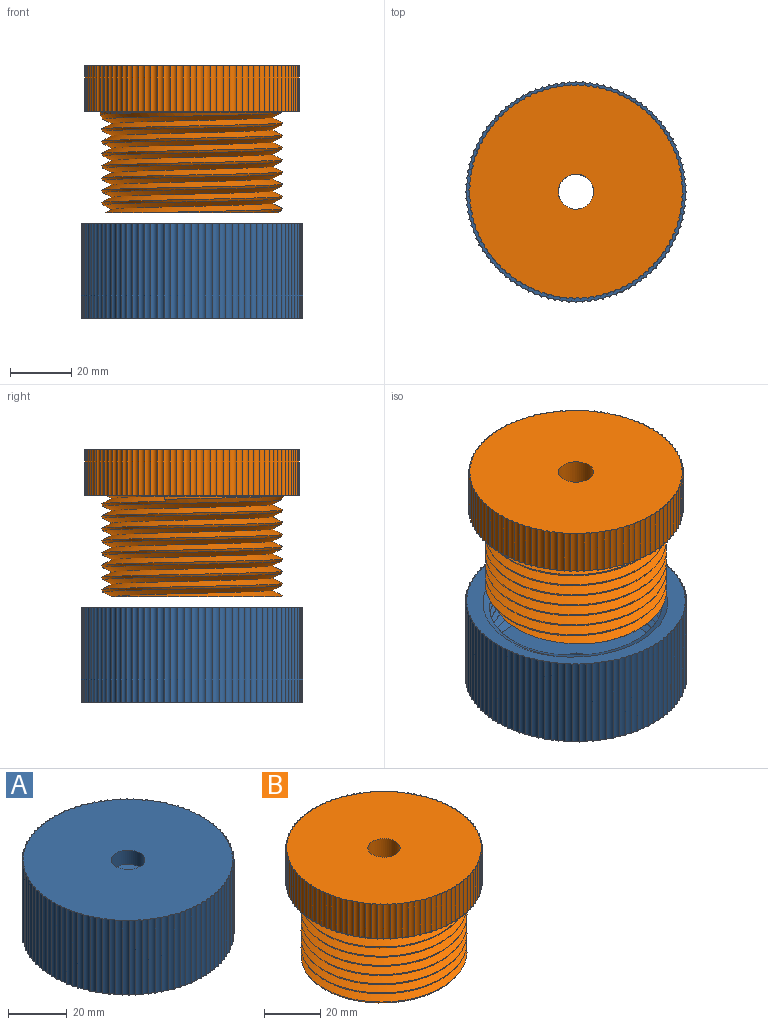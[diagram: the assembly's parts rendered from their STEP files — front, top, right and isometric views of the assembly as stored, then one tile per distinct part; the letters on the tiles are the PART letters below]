
ASSEMBLY  parts=2 mates=1
PART A: 107 faces, bbox 72.2x74.2x33.3 mm
  f0: bspline ~74.25x64.3mm, area 5175.7mm2, adj f1,f2,f3,f105
  f1: bspline ~74.25x64.3mm, area 5174.9mm2, adj f0,f2,f3,f105
  f2: cylinder r=28.25mm len=56.5mm, axis (0,0,-1), area 62.6mm2, adj f0,f1,f3,f105
  f3: plane 72.21x72.21mm, normal (0,0,-1), area 1161.6mm2, adj f0,f1,f2,f5,f6,f7,f8,f9
  f4: plane 72.21x72.21mm, normal (0,0,1), area 3917.8mm2, adj f5,f6,f7,f8,f9,f10,f11,f12
  f5: cylinder r=1.62mm len=31mm, axis (0,0,1), area 77.9mm2, adj f3,f4,f6,f104
  f6: cylinder r=1.62mm len=31mm, axis (0,0,1), area 77.9mm2, adj f3,f4,f5,f7
  f7: cylinder r=1.62mm len=31mm, axis (0,0,1), area 77.9mm2, adj f3,f4,f6,f8
  f8: cylinder r=1.62mm len=31mm, axis (0,0,1), area 77.9mm2, adj f3,f4,f7,f9
  f9: cylinder r=1.62mm len=31mm, axis (0,0,1), area 77.9mm2, adj f3,f4,f8,f10
  f10: cylinder r=1.62mm len=31mm, axis (0,0,1), area 77.9mm2, adj f3,f4,f9,f11
  f11: cylinder r=1.62mm len=31mm, axis (0,0,1), area 77.9mm2, adj f3,f4,f10,f12
  f12: cylinder r=1.62mm len=31mm, axis (0,0,1), area 77.9mm2, adj f3,f4,f11,f13
  f13: cylinder r=1.62mm len=31mm, axis (0,0,1), area 77.9mm2, adj f3,f4,f12,f14
  f14: cylinder r=1.62mm len=31mm, axis (0,0,1), area 77.9mm2, adj f3,f4,f13,f15
  f15: cylinder r=1.62mm len=31mm, axis (0,0,1), area 77.9mm2, adj f3,f4,f14,f16
  f16: cylinder r=1.62mm len=31mm, axis (0,0,1), area 77.9mm2, adj f3,f4,f15,f17
  f17: cylinder r=1.62mm len=31mm, axis (0,0,1), area 77.9mm2, adj f3,f4,f16,f18
  f18: cylinder r=1.62mm len=31mm, axis (0,0,1), area 77.9mm2, adj f3,f4,f17,f19
  f19: cylinder r=1.62mm len=31mm, axis (0,0,1), area 77.9mm2, adj f3,f4,f18,f20
  f20: cylinder r=1.62mm len=31mm, axis (0,0,1), area 77.9mm2, adj f3,f4,f19,f21
  f21: cylinder r=1.62mm len=31mm, axis (0,0,1), area 77.9mm2, adj f3,f4,f20,f22
  f22: cylinder r=1.62mm len=31mm, axis (0,0,1), area 77.9mm2, adj f3,f4,f21,f23
  f23: cylinder r=1.62mm len=31mm, axis (0,0,1), area 77.9mm2, adj f3,f4,f22,f24
  f24: cylinder r=1.62mm len=31mm, axis (0,0,1), area 77.9mm2, adj f3,f4,f23,f25
  f25: cylinder r=1.62mm len=31mm, axis (0,0,1), area 77.9mm2, adj f3,f4,f24,f26
  f26: cylinder r=1.62mm len=31mm, axis (0,0,1), area 77.9mm2, adj f3,f4,f25,f27
  f27: cylinder r=1.62mm len=31mm, axis (0,0,1), area 77.9mm2, adj f3,f4,f26,f28
  f28: cylinder r=1.62mm len=31mm, axis (0,0,1), area 77.9mm2, adj f3,f4,f27,f29
  f29: cylinder r=1.62mm len=31mm, axis (0,0,1), area 77.9mm2, adj f3,f4,f28,f30
  f30: cylinder r=1.62mm len=31mm, axis (0,0,1), area 77.9mm2, adj f3,f4,f29,f31
  f31: cylinder r=1.62mm len=31mm, axis (0,0,1), area 77.9mm2, adj f3,f4,f30,f32
  f32: cylinder r=1.62mm len=31mm, axis (0,0,1), area 77.9mm2, adj f3,f4,f31,f33
  f33: cylinder r=1.62mm len=31mm, axis (0,0,1), area 77.9mm2, adj f3,f4,f32,f34
  f34: cylinder r=1.62mm len=31mm, axis (0,0,1), area 77.9mm2, adj f3,f4,f33,f35
  f35: cylinder r=1.62mm len=31mm, axis (0,0,1), area 77.9mm2, adj f3,f4,f34,f36
  f36: cylinder r=1.62mm len=31mm, axis (0,0,1), area 77.9mm2, adj f3,f4,f35,f37
  f37: cylinder r=1.62mm len=31mm, axis (0,0,1), area 77.9mm2, adj f3,f4,f36,f38
  f38: cylinder r=1.62mm len=31mm, axis (0,0,1), area 77.9mm2, adj f3,f4,f37,f39
  f39: cylinder r=1.62mm len=31mm, axis (0,0,1), area 77.9mm2, adj f3,f4,f38,f40
  f40: cylinder r=1.62mm len=31mm, axis (0,0,1), area 77.9mm2, adj f3,f4,f39,f41
  f41: cylinder r=1.62mm len=31mm, axis (0,0,1), area 77.9mm2, adj f3,f4,f40,f42
  f42: cylinder r=1.62mm len=31mm, axis (0,0,1), area 77.9mm2, adj f3,f4,f41,f43
  f43: cylinder r=1.62mm len=31mm, axis (0,0,1), area 77.9mm2, adj f3,f4,f42,f44
  f44: cylinder r=1.62mm len=31mm, axis (0,0,1), area 77.9mm2, adj f3,f4,f43,f45
  f45: cylinder r=1.62mm len=31mm, axis (0,0,1), area 77.9mm2, adj f3,f4,f44,f46
  f46: cylinder r=1.62mm len=31mm, axis (0,0,1), area 77.9mm2, adj f3,f4,f45,f47
  f47: cylinder r=1.62mm len=31mm, axis (0,0,1), area 77.9mm2, adj f3,f4,f46,f48
  f48: cylinder r=1.62mm len=31mm, axis (0,0,1), area 77.9mm2, adj f3,f4,f47,f49
  f49: cylinder r=1.62mm len=31mm, axis (0,0,1), area 77.9mm2, adj f3,f4,f48,f50
  f50: cylinder r=1.62mm len=31mm, axis (0,0,1), area 77.9mm2, adj f3,f4,f49,f51
  f51: cylinder r=1.62mm len=31mm, axis (0,0,1), area 77.9mm2, adj f3,f4,f50,f52
  f52: cylinder r=1.62mm len=31mm, axis (0,0,1), area 77.9mm2, adj f3,f4,f51,f53
  f53: cylinder r=1.62mm len=31mm, axis (0,0,1), area 77.9mm2, adj f3,f4,f52,f54
  f54: cylinder r=1.62mm len=31mm, axis (0,0,1), area 77.9mm2, adj f3,f4,f53,f55
  f55: cylinder r=1.62mm len=31mm, axis (0,0,1), area 77.9mm2, adj f3,f4,f54,f56
  f56: cylinder r=1.62mm len=31mm, axis (0,0,1), area 77.9mm2, adj f3,f4,f55,f57
  f57: cylinder r=1.62mm len=31mm, axis (0,0,1), area 77.9mm2, adj f3,f4,f56,f58
  f58: cylinder r=1.62mm len=31mm, axis (0,0,1), area 77.9mm2, adj f3,f4,f57,f59
  f59: cylinder r=1.62mm len=31mm, axis (0,0,1), area 77.9mm2, adj f3,f4,f58,f60
  f60: cylinder r=1.62mm len=31mm, axis (0,0,1), area 77.9mm2, adj f3,f4,f59,f61
  f61: cylinder r=1.62mm len=31mm, axis (0,0,1), area 77.9mm2, adj f3,f4,f60,f62
  f62: cylinder r=1.62mm len=31mm, axis (0,0,1), area 77.9mm2, adj f3,f4,f61,f63
  f63: cylinder r=1.62mm len=31mm, axis (0,0,1), area 77.9mm2, adj f3,f4,f62,f64
  f64: cylinder r=1.62mm len=31mm, axis (0,0,1), area 77.9mm2, adj f3,f4,f63,f65
  f65: cylinder r=1.62mm len=31mm, axis (0,0,1), area 77.9mm2, adj f3,f4,f64,f66
  f66: cylinder r=1.62mm len=31mm, axis (0,0,1), area 77.9mm2, adj f3,f4,f65,f67
  f67: cylinder r=1.62mm len=31mm, axis (0,0,1), area 77.9mm2, adj f3,f4,f66,f68
  f68: cylinder r=1.62mm len=31mm, axis (0,0,1), area 77.9mm2, adj f3,f4,f67,f69
  f69: cylinder r=1.62mm len=31mm, axis (0,0,1), area 77.9mm2, adj f3,f4,f68,f70
  f70: cylinder r=1.62mm len=31mm, axis (0,0,1), area 77.9mm2, adj f3,f4,f69,f71
  f71: cylinder r=1.62mm len=31mm, axis (0,0,1), area 77.9mm2, adj f3,f4,f70,f72
  f72: cylinder r=1.62mm len=31mm, axis (0,0,1), area 77.9mm2, adj f3,f4,f71,f73
  f73: cylinder r=1.62mm len=31mm, axis (0,0,1), area 77.9mm2, adj f3,f4,f72,f74
  f74: cylinder r=1.62mm len=31mm, axis (0,0,1), area 77.9mm2, adj f3,f4,f73,f75
  f75: cylinder r=1.62mm len=31mm, axis (0,0,1), area 77.9mm2, adj f3,f4,f74,f76
  f76: cylinder r=1.62mm len=31mm, axis (0,0,1), area 77.9mm2, adj f3,f4,f75,f77
  f77: cylinder r=1.62mm len=31mm, axis (0,0,1), area 77.9mm2, adj f3,f4,f76,f78
  f78: cylinder r=1.62mm len=31mm, axis (0,0,1), area 77.9mm2, adj f3,f4,f77,f79
  f79: cylinder r=1.62mm len=31mm, axis (0,0,1), area 77.9mm2, adj f3,f4,f78,f80
  f80: cylinder r=1.62mm len=31mm, axis (0,0,1), area 77.9mm2, adj f3,f4,f79,f81
  f81: cylinder r=1.62mm len=31mm, axis (0,0,1), area 77.9mm2, adj f3,f4,f80,f82
  f82: cylinder r=1.62mm len=31mm, axis (0,0,1), area 77.9mm2, adj f3,f4,f81,f83
  f83: cylinder r=1.62mm len=31mm, axis (0,0,1), area 77.9mm2, adj f3,f4,f82,f84
  f84: cylinder r=1.62mm len=31mm, axis (0,0,1), area 77.9mm2, adj f3,f4,f83,f85
  f85: cylinder r=1.62mm len=31mm, axis (0,0,1), area 77.9mm2, adj f3,f4,f84,f86
  f86: cylinder r=1.62mm len=31mm, axis (0,0,1), area 77.9mm2, adj f3,f4,f85,f87
  f87: cylinder r=1.62mm len=31mm, axis (0,0,1), area 77.9mm2, adj f3,f4,f86,f88
  f88: cylinder r=1.62mm len=31mm, axis (0,0,1), area 77.9mm2, adj f3,f4,f87,f89
  f89: cylinder r=1.62mm len=31mm, axis (0,0,1), area 77.9mm2, adj f3,f4,f88,f90
  f90: cylinder r=1.62mm len=31mm, axis (0,0,1), area 77.9mm2, adj f3,f4,f89,f91
  f91: cylinder r=1.62mm len=31mm, axis (0,0,1), area 77.9mm2, adj f3,f4,f90,f92
  f92: cylinder r=1.62mm len=31mm, axis (0,0,1), area 77.9mm2, adj f3,f4,f91,f93
  f93: cylinder r=1.62mm len=31mm, axis (0,0,1), area 77.9mm2, adj f3,f4,f92,f94
  f94: cylinder r=1.62mm len=31mm, axis (0,0,1), area 77.9mm2, adj f3,f4,f93,f95
  f95: cylinder r=1.62mm len=31mm, axis (0,0,1), area 77.9mm2, adj f3,f4,f94,f96
  f96: cylinder r=1.62mm len=31mm, axis (0,0,1), area 77.9mm2, adj f3,f4,f95,f97
  f97: cylinder r=1.62mm len=31mm, axis (0,0,1), area 77.9mm2, adj f3,f4,f96,f98
  f98: cylinder r=1.62mm len=31mm, axis (0,0,1), area 77.9mm2, adj f3,f4,f97,f99
  f99: cylinder r=1.62mm len=31mm, axis (0,0,1), area 77.9mm2, adj f3,f4,f98,f100
  f100: cylinder r=1.62mm len=31mm, axis (0,0,1), area 77.9mm2, adj f3,f4,f99,f101
  f101: cylinder r=1.62mm len=31mm, axis (0,0,1), area 77.9mm2, adj f3,f4,f100,f102
  f102: cylinder r=1.62mm len=31mm, axis (0,0,1), area 77.9mm2, adj f3,f4,f101,f103
  f103: cylinder r=1.62mm len=31mm, axis (0,0,1), area 77.9mm2, adj f3,f4,f102,f104
  f104: cylinder r=1.62mm len=31mm, axis (0,0,1), area 77.9mm2, adj f3,f4,f5,f103
  f105: plane 60.4x60.37mm, normal (0,0,-1), area 2756.4mm2, adj f0,f1,f2,f106
  f106: cylinder r=5.75mm len=11.5mm, axis (0,0,1), area 216.8mm2, adj f4,f105
PART B: 195 faces, bbox 72.6x72.6x52.9 mm
  f0: cylinder r=1.62mm len=0.9mm, axis (0,0,1), area 0.1mm2, adj f26,f76,f85,f92
  f1: cylinder r=1.62mm len=1.8mm, axis (0,0,1), area 0.2mm2, adj f2,f74,f85,f92
  f2: cylinder r=1.62mm len=1.8mm, axis (0,0,1), area 0.2mm2, adj f1,f3,f85,f92
  f3: cylinder r=1.62mm len=1.8mm, axis (0,0,1), area 0.2mm2, adj f2,f4,f85,f92
  f4: cylinder r=1.62mm len=1.78mm, axis (0,0,1), area 0.2mm2, adj f3,f5,f85,f92
  f5: cylinder r=1.62mm len=1.77mm, axis (0,0,1), area 0.2mm2, adj f4,f6,f85,f92
  f6: cylinder r=1.62mm len=1.74mm, axis (0,0,1), area 0.2mm2, adj f5,f7,f85,f92
  f7: cylinder r=1.62mm len=1.71mm, axis (0,0,1), area 0.2mm2, adj f6,f8,f85,f92
  f8: cylinder r=1.62mm len=1.67mm, axis (0,0,1), area 0.2mm2, adj f7,f9,f85,f92
  f9: cylinder r=1.62mm len=1.63mm, axis (0,0,1), area 0.2mm2, adj f8,f10,f85,f92
  f10: cylinder r=1.62mm len=1.58mm, axis (0,0,1), area 0.2mm2, adj f9,f11,f85,f92
  f11: cylinder r=1.62mm len=1.52mm, axis (0,0,1), area 0.2mm2, adj f10,f12,f85,f92
  f12: cylinder r=1.62mm len=1.46mm, axis (0,0,1), area 0.2mm2, adj f11,f13,f85,f92
  f13: cylinder r=1.62mm len=1.39mm, axis (0,0,1), area 0.2mm2, adj f12,f14,f85,f92
  f14: cylinder r=1.62mm len=1.31mm, axis (0,0,1), area 0.2mm2, adj f13,f15,f85,f92
  f15: cylinder r=1.62mm len=1.31mm, axis (0,0,1), area 0.2mm2, adj f14,f16,f85,f92
  f16: cylinder r=1.62mm len=1.39mm, axis (0,0,1), area 0.2mm2, adj f15,f17,f85,f92
  f17: cylinder r=1.62mm len=1.46mm, axis (0,0,1), area 0.2mm2, adj f16,f18,f85,f92
  f18: cylinder r=1.62mm len=1.52mm, axis (0,0,1), area 0.2mm2, adj f17,f19,f85,f92
  f19: cylinder r=1.62mm len=1.58mm, axis (0,0,1), area 0.2mm2, adj f18,f20,f85,f92
  f20: cylinder r=1.62mm len=1.63mm, axis (0,0,1), area 0.2mm2, adj f19,f21,f85,f92
  f21: cylinder r=1.62mm len=1.67mm, axis (0,0,1), area 0.2mm2, adj f20,f22,f85,f92
  f22: cylinder r=1.62mm len=1.71mm, axis (0,0,1), area 0.2mm2, adj f21,f23,f85,f92
  f23: cylinder r=1.62mm len=1.74mm, axis (0,0,1), area 0.2mm2, adj f22,f24,f85,f92
  f24: cylinder r=1.62mm len=1.77mm, axis (0,0,1), area 0.2mm2, adj f23,f25,f85,f92
  f25: cylinder r=1.62mm len=1.78mm, axis (0,0,1), area 0.2mm2, adj f24,f26,f85,f92
  f26: cylinder r=1.62mm len=1.8mm, axis (0,0,1), area 0.2mm2, adj f0,f25,f85,f92
  f27: cylinder r=1.62mm len=0.73mm, axis (0,0,1), area 0mm2, adj f75,f92
  f28: cylinder r=1.62mm len=1.22mm, axis (0,0,1), area 0mm2, adj f75,f92
  f29: cylinder r=1.62mm len=1.54mm, axis (0,0,1), area 0.1mm2, adj f75,f92
  f30: cylinder r=1.62mm len=1.7mm, axis (0,0,1), area 0.2mm2, adj f31,f75,f86,f92
  f31: cylinder r=1.62mm len=1.71mm, axis (0,0,1), area 0.2mm2, adj f30,f32,f75,f87,f92
  f32: cylinder r=1.62mm len=1.67mm, axis (0,0,1), area 0.2mm2, adj f31,f33,f75,f88,f92
  f33: cylinder r=1.62mm len=1.63mm, axis (0,0,1), area 0.2mm2, adj f32,f34,f75,f85,f92
  f34: cylinder r=1.62mm len=1.58mm, axis (0,0,1), area 0.2mm2, adj f33,f35,f85,f92
  f35: cylinder r=1.62mm len=1.52mm, axis (0,0,1), area 0.2mm2, adj f34,f36,f85,f92
  f36: cylinder r=1.62mm len=1.46mm, axis (0,0,1), area 0.2mm2, adj f35,f37,f85,f92
  f37: cylinder r=1.62mm len=1.39mm, axis (0,0,1), area 0.2mm2, adj f36,f38,f85,f92
  f38: cylinder r=1.62mm len=1.31mm, axis (0,0,1), area 0.2mm2, adj f37,f39,f85,f92
  f39: cylinder r=1.62mm len=1.31mm, axis (0,0,1), area 0.2mm2, adj f38,f40,f85,f92
  f40: cylinder r=1.62mm len=1.39mm, axis (0,0,1), area 0.2mm2, adj f39,f41,f85,f92
  f41: cylinder r=1.62mm len=1.46mm, axis (0,0,1), area 0.2mm2, adj f40,f42,f85,f92
  f42: cylinder r=1.62mm len=1.52mm, axis (0,0,1), area 0.2mm2, adj f41,f43,f85,f92
  f43: cylinder r=1.62mm len=1.58mm, axis (0,0,1), area 0.2mm2, adj f42,f44,f85,f92
  f44: cylinder r=1.62mm len=1.63mm, axis (0,0,1), area 0.2mm2, adj f43,f45,f85,f92
  f45: cylinder r=1.62mm len=1.67mm, axis (0,0,1), area 0.2mm2, adj f44,f46,f85,f92
  f46: cylinder r=1.62mm len=1.71mm, axis (0,0,1), area 0.2mm2, adj f45,f47,f85,f92
  f47: cylinder r=1.62mm len=1.74mm, axis (0,0,1), area 0.2mm2, adj f46,f48,f85,f92
  f48: cylinder r=1.62mm len=1.77mm, axis (0,0,1), area 0.2mm2, adj f47,f49,f85,f92
  f49: cylinder r=1.62mm len=1.78mm, axis (0,0,1), area 0.2mm2, adj f48,f50,f85,f92
  f50: cylinder r=1.62mm len=1.8mm, axis (0,0,1), area 0.2mm2, adj f49,f51,f85,f92
  f51: cylinder r=1.62mm len=1.8mm, axis (0,0,1), area 0.2mm2, adj f50,f52,f85,f92
  f52: cylinder r=1.62mm len=1.8mm, axis (0,0,1), area 0.2mm2, adj f51,f53,f85,f92
  f53: cylinder r=1.62mm len=1.78mm, axis (0,0,1), area 0.2mm2, adj f52,f54,f85,f92
  f54: cylinder r=1.62mm len=1.77mm, axis (0,0,1), area 0.2mm2, adj f53,f55,f85,f92
  f55: cylinder r=1.62mm len=1.74mm, axis (0,0,1), area 0.2mm2, adj f54,f56,f85,f92
  f56: cylinder r=1.62mm len=1.71mm, axis (0,0,1), area 0.2mm2, adj f55,f57,f85,f92
  f57: cylinder r=1.62mm len=1.67mm, axis (0,0,1), area 0.2mm2, adj f56,f58,f85,f92
  f58: cylinder r=1.62mm len=1.63mm, axis (0,0,1), area 0.2mm2, adj f57,f59,f85,f92
  f59: cylinder r=1.62mm len=1.58mm, axis (0,0,1), area 0.2mm2, adj f58,f60,f85,f92
  f60: cylinder r=1.62mm len=1.52mm, axis (0,0,1), area 0.2mm2, adj f59,f61,f85,f92
  f61: cylinder r=1.62mm len=1.46mm, axis (0,0,1), area 0.2mm2, adj f60,f62,f85,f92
  f62: cylinder r=1.62mm len=1.39mm, axis (0,0,1), area 0.2mm2, adj f61,f63,f85,f92
  f63: cylinder r=1.62mm len=1.31mm, axis (0,0,1), area 0.2mm2, adj f62,f64,f85,f92
  f64: cylinder r=1.62mm len=1.31mm, axis (0,0,1), area 0.2mm2, adj f63,f65,f85,f92
  f65: cylinder r=1.62mm len=1.39mm, axis (0,0,1), area 0.2mm2, adj f64,f66,f85,f92
  f66: cylinder r=1.62mm len=1.46mm, axis (0,0,1), area 0.2mm2, adj f65,f67,f85,f92
  f67: cylinder r=1.62mm len=1.52mm, axis (0,0,1), area 0.2mm2, adj f66,f68,f85,f92
  f68: cylinder r=1.62mm len=1.58mm, axis (0,0,1), area 0.2mm2, adj f67,f69,f85,f92
  f69: cylinder r=1.62mm len=1.63mm, axis (0,0,1), area 0.2mm2, adj f68,f70,f85,f92
  f70: cylinder r=1.62mm len=1.67mm, axis (0,0,1), area 0.2mm2, adj f69,f71,f85,f92
  f71: cylinder r=1.62mm len=1.71mm, axis (0,0,1), area 0.2mm2, adj f70,f72,f85,f92
  f72: cylinder r=1.62mm len=1.74mm, axis (0,0,1), area 0.2mm2, adj f71,f73,f85,f92
  f73: cylinder r=1.62mm len=1.77mm, axis (0,0,1), area 0.2mm2, adj f72,f74,f85,f92
  f74: cylinder r=1.62mm len=1.78mm, axis (0,0,1), area 0.2mm2, adj f1,f73,f85,f92
  f75: bspline ~69.28x60mm, area 4815.5mm2, adj f27,f28,f29,f30,f31,f32,f33,f76
  f76: plane 3.9x1.84mm, normal (0,-1,0), area 3.8mm2, adj f0,f75,f83,f84,f85,f90,f92
  f77: plane 28x9.75mm, normal (-0.5,0.87,0), area 315.2mm2, adj f78,f82,f89,f91
  f78: plane 28x11.26mm, normal (-1,0,0), area 315.2mm2, adj f77,f79,f89,f91
  f79: plane 28x9.75mm, normal (-0.5,-0.87,0), area 315.2mm2, adj f78,f80,f89,f91
  f80: plane 28x9.75mm, normal (0.5,-0.87,0), area 315.2mm2, adj f79,f81,f89,f91
  f81: plane 28x11.26mm, normal (1,0,0), area 315.2mm2, adj f80,f82,f89,f91
  f82: plane 28x9.75mm, normal (0.5,0.87,0), area 315.2mm2, adj f77,f81,f89,f91
  f83: cylinder r=30mm len=32.24mm, axis (0,0,-1), area 26mm2, adj f76,f85,f90
  f84: bspline ~69.28x60mm, area 5428.3mm2, adj f75,f76,f89,f90
  f85: plane 60.05x56.8mm, normal (0,0,1), area 153.4mm2, adj f0,f1,f2,f3,f4,f5,f6,f7
  f86: plane 0.99x0.22mm, normal (0,0,1), area 0.1mm2, adj f30,f75
  f87: plane 1.35x0.4mm, normal (0,0,1), area 0.2mm2, adj f31,f75
  f88: plane 1.59x0.59mm, normal (0,0,1), area 0.3mm2, adj f32,f75
  f89: plane 58.76x58.45mm, normal (0,0,-1), area 2143.5mm2, adj f75,f77,f78,f79,f80,f81,f82,f84
  f90: bspline ~59.98x59.91mm, area 1406.2mm2, adj f75,f76,f83,f84,f85,f89
  f91: plane 22.52x19.5mm, normal (0,0,-1), area 225.4mm2, adj f77,f78,f79,f80,f81,f82,f194
  f92: plane 70.16x70.16mm, normal (0,0,-1), area 1306.9mm2, adj f0,f1,f2,f3,f4,f5,f6,f7
  f93: cylinder r=1.62mm len=15mm, axis (0,0,1), area 36.4mm2, adj f92,f94,f192,f193
  f94: cylinder r=1.62mm len=15mm, axis (0,0,1), area 36.4mm2, adj f92,f93,f95,f193
  f95: cylinder r=1.62mm len=15mm, axis (0,0,1), area 36.4mm2, adj f92,f94,f96,f193
  f96: cylinder r=1.62mm len=15mm, axis (0,0,1), area 36.4mm2, adj f92,f95,f97,f193
  f97: cylinder r=1.62mm len=15mm, axis (0,0,1), area 36.4mm2, adj f92,f96,f98,f193
  f98: cylinder r=1.62mm len=15mm, axis (0,0,1), area 36.4mm2, adj f92,f97,f99,f193
  f99: cylinder r=1.62mm len=15mm, axis (0,0,1), area 36.4mm2, adj f92,f98,f100,f193
  f100: cylinder r=1.62mm len=15mm, axis (0,0,1), area 36.4mm2, adj f92,f99,f101,f193
  f101: cylinder r=1.62mm len=15mm, axis (0,0,1), area 36.4mm2, adj f92,f100,f102,f193
  f102: cylinder r=1.62mm len=15mm, axis (0,0,1), area 36.4mm2, adj f92,f101,f103,f193
  f103: cylinder r=1.62mm len=15mm, axis (0,0,1), area 36.4mm2, adj f92,f102,f104,f193
  f104: cylinder r=1.62mm len=15mm, axis (0,0,1), area 36.4mm2, adj f92,f103,f105,f193
  f105: cylinder r=1.62mm len=15mm, axis (0,0,1), area 36.4mm2, adj f92,f104,f106,f193
  f106: cylinder r=1.62mm len=15mm, axis (0,0,1), area 36.4mm2, adj f92,f105,f107,f193
  f107: cylinder r=1.62mm len=15mm, axis (0,0,1), area 36.4mm2, adj f92,f106,f108,f193
  f108: cylinder r=1.62mm len=15mm, axis (0,0,1), area 36.4mm2, adj f92,f107,f109,f193
  f109: cylinder r=1.62mm len=15mm, axis (0,0,1), area 36.4mm2, adj f92,f108,f110,f193
  f110: cylinder r=1.62mm len=15mm, axis (0,0,1), area 36.4mm2, adj f92,f109,f111,f193
  f111: cylinder r=1.62mm len=15mm, axis (0,0,1), area 36.4mm2, adj f92,f110,f112,f193
  f112: cylinder r=1.62mm len=15mm, axis (0,0,1), area 36.4mm2, adj f92,f111,f113,f193
  f113: cylinder r=1.62mm len=15mm, axis (0,0,1), area 36.4mm2, adj f92,f112,f114,f193
  f114: cylinder r=1.62mm len=15mm, axis (0,0,1), area 36.4mm2, adj f92,f113,f115,f193
  f115: cylinder r=1.62mm len=15mm, axis (0,0,1), area 36.4mm2, adj f92,f114,f116,f193
  f116: cylinder r=1.62mm len=15mm, axis (0,0,1), area 36.4mm2, adj f92,f115,f117,f193
  f117: cylinder r=1.62mm len=15mm, axis (0,0,1), area 36.4mm2, adj f92,f116,f118,f193
  f118: cylinder r=1.62mm len=15mm, axis (0,0,1), area 36.4mm2, adj f92,f117,f119,f193
  f119: cylinder r=1.62mm len=15mm, axis (0,0,1), area 36.4mm2, adj f92,f118,f120,f193
  f120: cylinder r=1.62mm len=15mm, axis (0,0,1), area 36.4mm2, adj f92,f119,f121,f193
  f121: cylinder r=1.62mm len=15mm, axis (0,0,1), area 36.4mm2, adj f92,f120,f122,f193
  f122: cylinder r=1.62mm len=15mm, axis (0,0,1), area 36.4mm2, adj f92,f121,f123,f193
  f123: cylinder r=1.62mm len=15mm, axis (0,0,1), area 36.4mm2, adj f92,f122,f124,f193
  f124: cylinder r=1.62mm len=15mm, axis (0,0,1), area 36.4mm2, adj f92,f123,f125,f193
  f125: cylinder r=1.62mm len=15mm, axis (0,0,1), area 36.4mm2, adj f92,f124,f126,f193
  f126: cylinder r=1.62mm len=15mm, axis (0,0,1), area 36.4mm2, adj f92,f125,f127,f193
  f127: cylinder r=1.62mm len=15mm, axis (0,0,1), area 36.4mm2, adj f92,f126,f128,f193
  f128: cylinder r=1.62mm len=15mm, axis (0,0,1), area 36.4mm2, adj f92,f127,f129,f193
  f129: cylinder r=1.62mm len=15mm, axis (0,0,1), area 36.4mm2, adj f92,f128,f130,f193
  f130: cylinder r=1.62mm len=15mm, axis (0,0,1), area 36.4mm2, adj f92,f129,f131,f193
  f131: cylinder r=1.62mm len=15mm, axis (0,0,1), area 36.4mm2, adj f92,f130,f132,f193
  f132: cylinder r=1.62mm len=15mm, axis (0,0,1), area 36.4mm2, adj f92,f131,f133,f193
  f133: cylinder r=1.62mm len=15mm, axis (0,0,1), area 36.4mm2, adj f92,f132,f134,f193
  f134: cylinder r=1.62mm len=15mm, axis (0,0,1), area 36.4mm2, adj f92,f133,f135,f193
  f135: cylinder r=1.62mm len=15mm, axis (0,0,1), area 36.4mm2, adj f92,f134,f136,f193
  f136: cylinder r=1.62mm len=15mm, axis (0,0,1), area 36.4mm2, adj f92,f135,f137,f193
  f137: cylinder r=1.62mm len=15mm, axis (0,0,1), area 36.4mm2, adj f92,f136,f138,f193
  f138: cylinder r=1.62mm len=15mm, axis (0,0,1), area 36.4mm2, adj f92,f137,f139,f193
  f139: cylinder r=1.62mm len=15mm, axis (0,0,1), area 36.4mm2, adj f92,f138,f140,f193
  f140: cylinder r=1.62mm len=15mm, axis (0,0,1), area 36.4mm2, adj f92,f139,f141,f193
  f141: cylinder r=1.62mm len=15mm, axis (0,0,1), area 36.4mm2, adj f92,f140,f142,f193
  f142: cylinder r=1.62mm len=15mm, axis (0,0,1), area 36.4mm2, adj f92,f141,f143,f193
  f143: cylinder r=1.62mm len=15mm, axis (0,0,1), area 36.4mm2, adj f92,f142,f144,f193
  f144: cylinder r=1.62mm len=15mm, axis (0,0,1), area 36.4mm2, adj f92,f143,f145,f193
  f145: cylinder r=1.62mm len=15mm, axis (0,0,1), area 36.4mm2, adj f92,f144,f146,f193
  f146: cylinder r=1.62mm len=15mm, axis (0,0,1), area 36.4mm2, adj f92,f145,f147,f193
  f147: cylinder r=1.62mm len=15mm, axis (0,0,1), area 36.4mm2, adj f92,f146,f148,f193
  f148: cylinder r=1.62mm len=15mm, axis (0,0,1), area 36.4mm2, adj f92,f147,f149,f193
  f149: cylinder r=1.62mm len=15mm, axis (0,0,1), area 36.4mm2, adj f92,f148,f150,f193
  f150: cylinder r=1.62mm len=15mm, axis (0,0,1), area 36.4mm2, adj f92,f149,f151,f193
  f151: cylinder r=1.62mm len=15mm, axis (0,0,1), area 36.4mm2, adj f92,f150,f152,f193
  f152: cylinder r=1.62mm len=15mm, axis (0,0,1), area 36.4mm2, adj f92,f151,f153,f193
  f153: cylinder r=1.62mm len=15mm, axis (0,0,1), area 36.4mm2, adj f92,f152,f154,f193
  f154: cylinder r=1.62mm len=15mm, axis (0,0,1), area 36.4mm2, adj f92,f153,f155,f193
  f155: cylinder r=1.62mm len=15mm, axis (0,0,1), area 36.4mm2, adj f92,f154,f156,f193
  f156: cylinder r=1.62mm len=15mm, axis (0,0,1), area 36.4mm2, adj f92,f155,f157,f193
  f157: cylinder r=1.62mm len=15mm, axis (0,0,1), area 36.4mm2, adj f92,f156,f158,f193
  f158: cylinder r=1.62mm len=15mm, axis (0,0,1), area 36.4mm2, adj f92,f157,f159,f193
  f159: cylinder r=1.62mm len=15mm, axis (0,0,1), area 36.4mm2, adj f92,f158,f160,f193
  f160: cylinder r=1.62mm len=15mm, axis (0,0,1), area 36.4mm2, adj f92,f159,f161,f193
  f161: cylinder r=1.62mm len=15mm, axis (0,0,1), area 36.4mm2, adj f92,f160,f162,f193
  f162: cylinder r=1.62mm len=15mm, axis (0,0,1), area 36.4mm2, adj f92,f161,f163,f193
  f163: cylinder r=1.62mm len=15mm, axis (0,0,1), area 36.4mm2, adj f92,f162,f164,f193
  f164: cylinder r=1.62mm len=15mm, axis (0,0,1), area 36.4mm2, adj f92,f163,f165,f193
  f165: cylinder r=1.62mm len=15mm, axis (0,0,1), area 36.4mm2, adj f92,f164,f166,f193
  f166: cylinder r=1.62mm len=15mm, axis (0,0,1), area 36.4mm2, adj f92,f165,f167,f193
  f167: cylinder r=1.62mm len=15mm, axis (0,0,1), area 36.4mm2, adj f92,f166,f168,f193
  f168: cylinder r=1.62mm len=15mm, axis (0,0,1), area 36.4mm2, adj f92,f167,f169,f193
  f169: cylinder r=1.62mm len=15mm, axis (0,0,1), area 36.4mm2, adj f92,f168,f170,f193
  f170: cylinder r=1.62mm len=15mm, axis (0,0,1), area 36.4mm2, adj f92,f169,f171,f193
  f171: cylinder r=1.62mm len=15mm, axis (0,0,1), area 36.4mm2, adj f92,f170,f172,f193
  f172: cylinder r=1.62mm len=15mm, axis (0,0,1), area 36.4mm2, adj f92,f171,f173,f193
  f173: cylinder r=1.62mm len=15mm, axis (0,0,1), area 36.4mm2, adj f92,f172,f174,f193
  f174: cylinder r=1.62mm len=15mm, axis (0,0,1), area 36.4mm2, adj f92,f173,f175,f193
  f175: cylinder r=1.62mm len=15mm, axis (0,0,1), area 36.4mm2, adj f92,f174,f176,f193
  f176: cylinder r=1.62mm len=15mm, axis (0,0,1), area 36.4mm2, adj f92,f175,f177,f193
  f177: cylinder r=1.62mm len=15mm, axis (0,0,1), area 36.4mm2, adj f92,f176,f178,f193
  f178: cylinder r=1.62mm len=15mm, axis (0,0,1), area 36.4mm2, adj f92,f177,f179,f193
  f179: cylinder r=1.62mm len=15mm, axis (0,0,1), area 36.4mm2, adj f92,f178,f180,f193
  f180: cylinder r=1.62mm len=15mm, axis (0,0,1), area 36.4mm2, adj f92,f179,f181,f193
  f181: cylinder r=1.62mm len=15mm, axis (0,0,1), area 36.4mm2, adj f92,f180,f182,f193
  f182: cylinder r=1.62mm len=15mm, axis (0,0,1), area 36.4mm2, adj f92,f181,f183,f193
  f183: cylinder r=1.62mm len=15mm, axis (0,0,1), area 36.4mm2, adj f92,f182,f184,f193
  f184: cylinder r=1.62mm len=15mm, axis (0,0,1), area 36.4mm2, adj f92,f183,f185,f193
  f185: cylinder r=1.62mm len=15mm, axis (0,0,1), area 36.4mm2, adj f92,f184,f186,f193
  f186: cylinder r=1.62mm len=15mm, axis (0,0,1), area 36.4mm2, adj f92,f185,f187,f193
  f187: cylinder r=1.62mm len=15mm, axis (0,0,1), area 36.4mm2, adj f92,f186,f188,f193
  f188: cylinder r=1.62mm len=15mm, axis (0,0,1), area 36.4mm2, adj f92,f187,f189,f193
  f189: cylinder r=1.62mm len=15mm, axis (0,0,1), area 36.4mm2, adj f92,f188,f190,f193
  f190: cylinder r=1.62mm len=15mm, axis (0,0,1), area 36.4mm2, adj f92,f189,f191,f193
  f191: cylinder r=1.62mm len=15mm, axis (0,0,1), area 36.4mm2, adj f92,f190,f192,f193
  f192: cylinder r=1.62mm len=15mm, axis (0,0,1), area 36.4mm2, adj f92,f93,f191,f193
  f193: plane 70.13x70.13mm, normal (0,0,1), area 3694.1mm2, adj f93,f94,f95,f96,f97,f98,f99,f100
  f194: cylinder r=5.75mm len=20mm, axis (0,0,1), area 722.6mm2, adj f91,f193
PLACE A rot(axis=(0.89,-0.46,0),180deg) t=(115.3,-64.68,-37.84)mm fixed
PLACE B rot(axis=(0,0,1),162.8deg) t=(115.3,-64.68,-59.42)mm
MATE cylindrical B.f83 <-> A.f2  axis (0,0,1) through (115.3,-64.68,-9.42)mm
